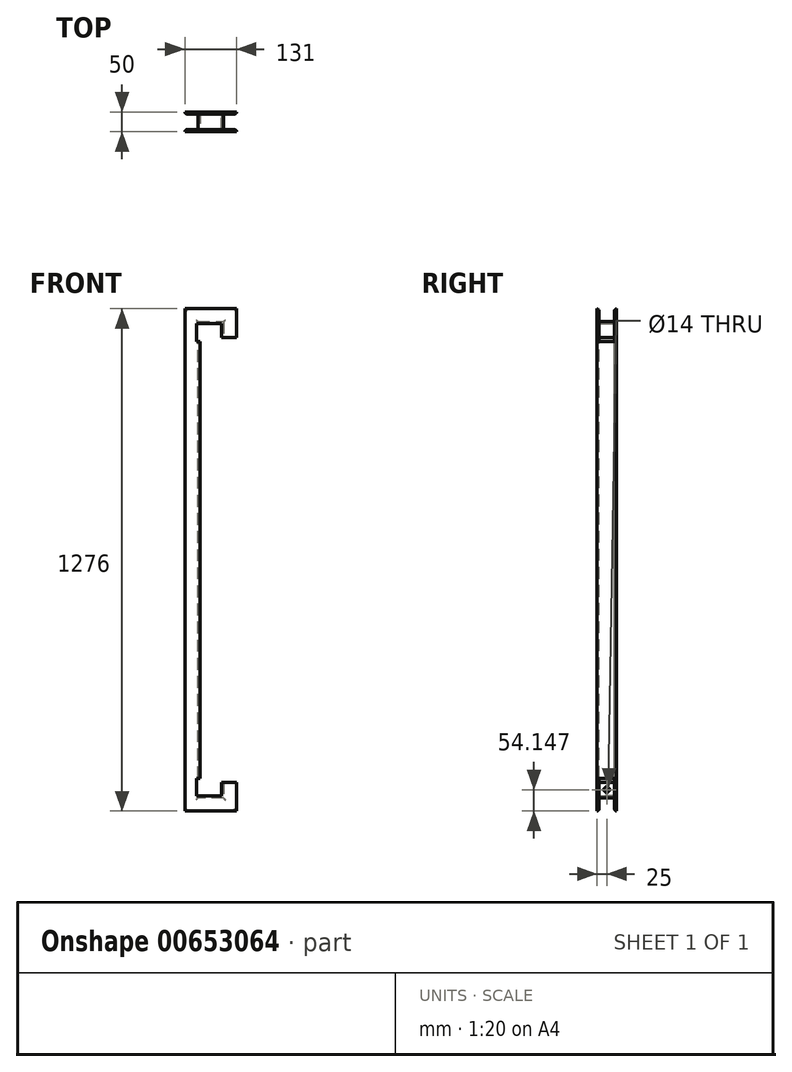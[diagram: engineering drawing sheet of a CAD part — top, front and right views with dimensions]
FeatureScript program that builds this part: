
annotation { "Feature Type Name" : "Feature", "Feature Type Description" : "" }
export const myFeature = defineFeature(function(context is Context, id is Id, definition is map)
    precondition{}
    {
        {
            var Q0;
            Q0=qCreatedBy(makeId("Top.planeOp"),FACE);
            var sketch = newSketch(context, id + "F0", { "sketchPlane" : qUnion([Q0])});
            skLineSegment(sketch, "E0.0", {"start": v(0, 0) * mm, "end": v(38, 0) * mm});
            skLineSegment(sketch, "E0.1", {"start": v(0, 50) * mm, "end": v(38, 50) * mm});
            skLineSegment(sketch, "E0.2", {"start": v(0, 0) * mm, "end": v(0, 50) * mm});
            skLineSegment(sketch, "E1.0", {"start": v(10, 45) * mm, "end": v(33, 45) * mm});
            skLineSegment(sketch, "E1.1", {"start": v(5, 10) * mm, "end": v(5, 40) * mm});
            skLineSegment(sketch, "E1.2", {"start": v(10, 5) * mm, "end": v(33, 5) * mm});
            skPoint(sketch, "E2.visualSharp", {"position": v(5, 45) * mm});
            skArc(sketch, "E2.filletArc", {"start": v(10, 45) * mm, "mid": v(6.46, 43.54) * mm, "end": v(5, 40) * mm});
            skPoint(sketch, "E3.visualSharp", {"position": v(5, 5) * mm});
            skArc(sketch, "E3.filletArc", {"start": v(5, 10) * mm, "mid": v(6.46, 6.46) * mm, "end": v(10, 5) * mm});
            skLineSegment(sketch, "E4", {"start": v(38, 0) * mm, "end": v(38, 0) * mm});
            skLineSegment(sketch, "E5", {"start": v(38, 50) * mm, "end": v(38, 50) * mm});
            skPoint(sketch, "E6.visualSharp", {"position": v(38, 45) * mm});
            skArc(sketch, "E6.filletArc", {"start": v(33, 45) * mm, "mid": v(36.54, 46.46) * mm, "end": v(38, 50) * mm});
            skPoint(sketch, "E7.visualSharp", {"position": v(38, 5) * mm});
            skArc(sketch, "E7.filletArc", {"start": v(38, 0) * mm, "mid": v(36.54, 3.54) * mm, "end": v(33, 5) * mm});
            skSolve(sketch);
        }
        {
            var Q0;
            Q0=qCreatedBy(makeId("Front.planeOp"),FACE);
            var sketch = newSketch(context, id + "F1", { "sketchPlane" : qUnion([Q0])});
            skLineSegment(sketch, "E8", {"start": v(0, 0) * mm, "end": v(0, -35) * mm});
            skLineSegment(sketch, "E9", {"start": v(0, -35) * mm, "end": v(-55, -35) * mm});
            skLineSegment(sketch, "E10", {"start": v(-55, -35) * mm, "end": v(-55, 1165) * mm});
            skLineSegment(sketch, "E11", {"start": v(-55, 1165) * mm, "end": v(0, 1165) * mm});
            skLineSegment(sketch, "E12", {"start": v(0, 1165) * mm, "end": v(0, 1130) * mm});
            skSolve(sketch);
        }
        {
            var Q0;
            Q0 = qSketchRegion(id + "F0", true);
            var Q1;
            Q1 = qConstructionFilter(qBodyType(qCreatedBy(id + "F1" ,EDGE), BodyType.WIRE), ConstructionObject.NO);
            sweep(context, id + "F2", {"profiles" : qUnion([Q0]), "path" : qUnion([Q1])});
        }
        {
            var Q0;
            Q0=makeQuery(id+"F2.opSweep","SWEPT_FACE",FACE,{"disambiguationData":[OSD([sQuery(id+"F0.wireOp",EDGE,"E0.0"),sQuery(id+"F1.wireOp",EDGE,"E10")])]});
            var sketch = newSketch(context, id + "F3", { "sketchPlane" : qUnion([Q0])});
            skLineSegment(sketch, "E13", {"start": v(-55, 565) * mm, "end": v(120.68, 565) * mm, "construction": true});
            skLineSegment(sketch, "E14.bottom", {"start": v(-27.5, 1120) * mm, "end": v(-63, 1120) * mm});
            skLineSegment(sketch, "E14.top", {"start": v(-27.5, 1165) * mm, "end": v(-63, 1165) * mm});
            skLineSegment(sketch, "E14.left", {"start": v(-27.5, 1120) * mm, "end": v(-27.5, 1165) * mm});
            skLineSegment(sketch, "E14.right", {"start": v(-63, 1120) * mm, "end": v(-63, 1165) * mm});
            skLineSegment(sketch, "E15.MirrorCS", {"start": v(-27.5, 10) * mm, "end": v(-63, 10) * mm});
            skLineSegment(sketch, "E16.MirrorCS", {"start": v(-27.5, -35) * mm, "end": v(-63, -35) * mm});
            skLineSegment(sketch, "E17.MirrorCS", {"start": v(-27.5, 10) * mm, "end": v(-27.5, -35) * mm});
            skLineSegment(sketch, "E18.MirrorCS", {"start": v(-63, 10) * mm, "end": v(-63, -35) * mm});
            skSolve(sketch);
        }
        {
            var Q0;
            Q0 = qSketchRegion(id + "F3", true);
            extrude(context, id + "F4", {"entities" : qUnion([Q0]), "operationType" : NewBodyOperationType.REMOVE, "endBound" : BoundingType.THROUGH_ALL, "oppositeDirection" : true, "depth" : 25 * mm, "offsetDistance" : 25 * mm});
        }
        {
            var Q0;
            Q0=makeQuery(id+"F2.opSweep","SWEPT_FACE",FACE,{"disambiguationData":[OSD([sQuery(id+"F0.wireOp",EDGE,"E1.1"),sQuery(id+"F1.wireOp",EDGE,"E12")])]});
            var sketch = newSketch(context, id + "F5", { "sketchPlane" : qUnion([Q0])});
            skLineSegment(sketch, "E19", {"start": v(25, 1170) * mm, "end": v(25, -38.54) * mm, "construction": true});
            skPoint(sketch, "E20", {"position": v(25, -18.85) * mm});
            skLineSegment(sketch, "E21", {"start": v(25, 565.73) * mm, "end": v(271.3, 565.73) * mm, "construction": true});
            skSolve(sketch);
        }
        {
            var Q0;
            Q0=sQuery(id+"F5.wireOp",VERTEX,"E20");
            var Q1;
            Q1=makeQuery(id+"F2.opSweep","SWEPT_BODY",BODY,{"disambiguationData":[OSD([sQuery(id+"F0.wireOp",EDGE,"E0.0"),sQuery(id+"F0.wireOp",EDGE,"E0.1"),sQuery(id+"F0.wireOp",EDGE,"E0.2"),sQuery(id+"F0.wireOp",EDGE,"E1.0"),sQuery(id+"F0.wireOp",EDGE,"E1.1"),sQuery(id+"F0.wireOp",EDGE,"E1.2"),sQuery(id+"F0.wireOp",EDGE,"E2.filletArc"),sQuery(id+"F0.wireOp",EDGE,"E3.filletArc"),sQuery(id+"F0.wireOp",EDGE,"E6.filletArc"),sQuery(id+"F0.wireOp",EDGE,"E7.filletArc"),sQuery(id+"F1.wireOp",EDGE,"E12")])]});
            hole(context, id + "F6", {"style" : HoleStyle.SIMPLE, "endStyle" : HoleEndStyle.THROUGH, "standardTappedOrClearance" : lookupTablePath({ "standard" : "ISO", "engagement" : "75%", "pitch" : "2 mm", "size" : "M16", "type" : "Tapped" }), "standardBlindInLast" : lookupTablePath({ "standard" : "ISO", "engagement" : "75%", "pitch" : "2 mm", "size" : "M16", "type" : "Tapped" }), "holeDiameter" : 14 * mm, "majorDiameter" : 16 * mm, "showTappedDepth" : true, "isTappedThrough" : true, "tappedDepth" : 12 * mm, "tapClearance" : 3, "locations" : qUnion([Q0]), "scope" : qUnion([Q1])});
        }
        {
            var Q0;
            Q0=makeQuery(id+"F2.opSweep","SWEPT_EDGE",EDGE,{"disambiguationData":[OSD([sQuery(id+"F0.wireOp",EDGE,"E0.1"),sQuery(id+"F0.wireOp",EDGE,"E0.2"),sQuery(id+"F1.wireOp",EDGE,"E10")])]});
            cPoint(context, id + "F7", {"entities" : qUnion([Q0]), "parameter" : 0.5});
        }
        {
            var Q0;
            Q0=qCreatedBy(makeId("Top.planeOp"),FACE);
            var Q1;
            Q1 = qCreatedBy(id + "F7" ,VERTEX);
            cPlane(context, id + "F8", {"entities" : qUnion([Q0, Q1]), "cplaneType" : CPlaneType.PLANE_POINT, "offset" : 25 * mm, "width" : 150 * mm, "height" : 150 * mm});
        }
    });
